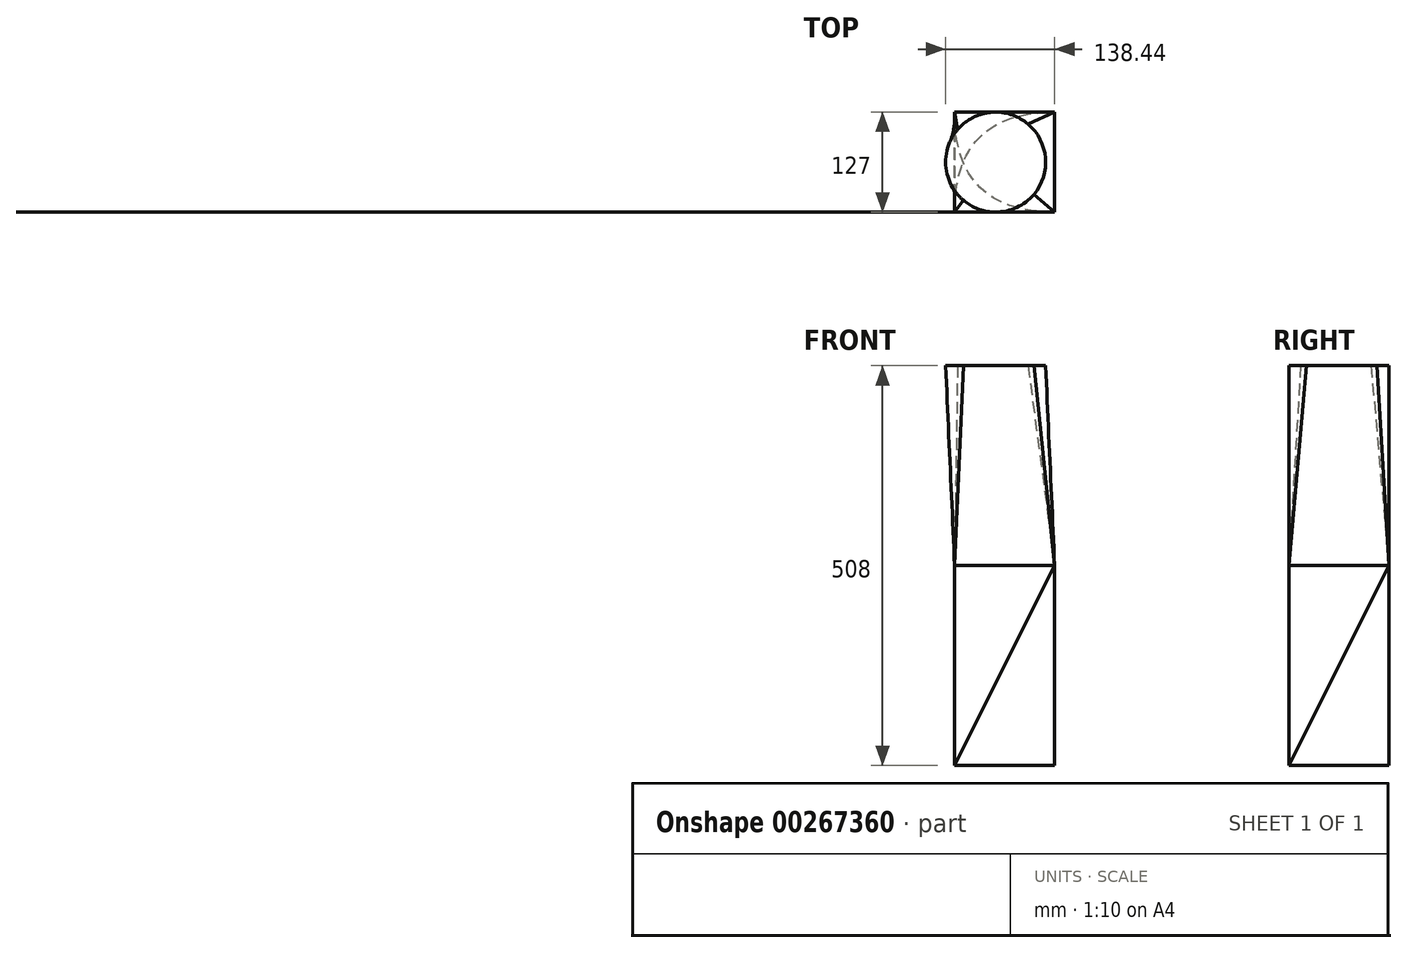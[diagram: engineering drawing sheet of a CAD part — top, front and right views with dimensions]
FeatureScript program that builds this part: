
annotation { "Feature Type Name" : "Feature", "Feature Type Description" : "" }
export const myFeature = defineFeature(function(context is Context, id is Id, definition is map)
    precondition{}
    {
        {
            var Q0;
            Q0=qCreatedBy(makeId("Top.planeOp"),FACE);
            var sketch = newSketch(context, id + "F0", { "sketchPlane" : qUnion([Q0])});
            skLineSegment(sketch, "E0.bottom", {"start": v(63.5, -63.5) * mm, "end": v(-63.5, -63.5) * mm});
            skLineSegment(sketch, "E0.top", {"start": v(63.5, 63.5) * mm, "end": v(-63.5, 63.5) * mm});
            skLineSegment(sketch, "E0.left", {"start": v(63.5, -63.5) * mm, "end": v(63.5, 63.5) * mm});
            skLineSegment(sketch, "E0.right", {"start": v(-63.5, -63.5) * mm, "end": v(-63.5, 63.5) * mm});
            skPoint(sketch, "E0.middle", {"position": v(0, 0) * mm});
            skSolve(sketch);
        }
        {
            var Q0;
            Q0=qCreatedBy(makeId("Top.planeOp"),FACE);
            cPlane(context, id + "F1", {"entities" : qUnion([Q0]), "cplaneType" : CPlaneType.OFFSET, "offset" : 254 * mm, "width" : 152.4 * mm, "height" : 152.4 * mm});
        }
        {
            var Q0;
            Q0=qCreatedBy(id+"F1.planeOp",FACE);
            var sketch = newSketch(context, id + "F2", { "sketchPlane" : qUnion([Q0])});
            skCircle(sketch, "E1", {"center": v(-11.44, 0) * mm, "radius": 63.5 * mm});
            skSolve(sketch);
        }
        {
            var Q0;
            Q0=qCreatedBy(makeId("Top.planeOp"),FACE);
            cPlane(context, id + "F3", {"entities" : qUnion([Q0]), "cplaneType" : CPlaneType.OFFSET, "offset" : 254 * mm, "oppositeDirection" : true, "width" : 152.4 * mm, "height" : 152.4 * mm});
        }
        {
            var Q0;
            Q0=qCreatedBy(id+"F3.planeOp",FACE);
            var sketch = newSketch(context, id + "F4", { "sketchPlane" : qUnion([Q0])});
            skLineSegment(sketch, "E2.bottom", {"start": v(63.5, -63.5) * mm, "end": v(-63.5, -63.5) * mm});
            skLineSegment(sketch, "E2.top", {"start": v(63.5, 63.5) * mm, "end": v(-63.5, 63.5) * mm});
            skLineSegment(sketch, "E2.left", {"start": v(63.5, -63.5) * mm, "end": v(63.5, 63.5) * mm});
            skLineSegment(sketch, "E2.right", {"start": v(-63.5, -63.5) * mm, "end": v(-63.5, 63.5) * mm});
            skPoint(sketch, "E2.middle", {"position": v(0, 0) * mm});
            skSolve(sketch);
        }
        {
            var Q0;
            Q0=makeQuery(id+"F4.imprint","IMPRINT",FACE,{"disambiguationData":[TD([[makeQuery(id+"F4.imprint","IMPRINT",EDGE,{"derivedFrom":sQuery(id+"F4.wireOp",EDGE,"E2.bottom")}),-1.0]])]});
            var Q1;
            Q1=makeQuery(id+"F0.imprint","IMPRINT",FACE,{"disambiguationData":[TD([[makeQuery(id+"F0.imprint","IMPRINT",EDGE,{"derivedFrom":sQuery(id+"F0.wireOp",EDGE,"E0.bottom")}),-1.0]])]});
            var Q2;
            Q2=sQuery(id+"F4.wireOp",VERTEX,"E2.right.start");
            var Q3;
            Q3=sQuery(id+"F0.wireOp",VERTEX,"E0.bottom.start");
            loft(context, id + "F5", {"sheetProfilesArray" : [{ "sheetProfileEntities" : qUnion([Q0]) }, { "sheetProfileEntities" : qUnion([Q1]) }], "matchConnections" : true, "connections" : [{ "connectionEntities" : qUnion([Q2, Q3]), "connectionEdgeQueries" : qUnion([]), "connectionEdgeParameters" : [] }]});
        }
        {
            var Q1;
            Q1=makeQuery(id+"F2.imprint","IMPRINT",FACE,{"disambiguationData":[TD([[makeQuery(id+"F2.imprint","IMPRINT",EDGE,{"derivedFrom":sQuery(id+"F2.wireOp",EDGE,"E1")}),1.0]])]});
            var Q2;
            Q2=makeQuery(id+"F5.opLoft","CAP_FACE",FACE,{"disambiguationData":[OSD([makeQuery(id+"F0.imprint","IMPRINT",FACE,{"disambiguationData":[TD([[makeQuery(id+"F0.imprint","IMPRINT",EDGE,{"derivedFrom":sQuery(id+"F0.wireOp",EDGE,"E0.bottom")}),-1.0]])]})])],"isStart":true});
            loft(context, id + "F6", {"operationType" : NewBodyOperationType.ADD, "sheetProfilesArray" : [{ "sheetProfileEntities" : qUnion([Q1]) }, { "sheetProfileEntities" : qUnion([Q2]) }]});
        }
    });
